# Revit family: IS_Connect_E5048_BIM_DE
name_source: partatom
category: Plumbing Fixtures
revit_build: Autodesk Revit 2016 (Build: 20150220_1215(x64)
units: mm (PartAtom-declared; Revit-internal decimal feet)

## family parameters
Cut with Voids When Loaded = Yes
Host = Face
OmniClass Number = 23.45.05.14.14
OmniClass Title = Sinks/Lavatories
Part Type = Normal
Room Calculation Point = No
Round Connector Dimension = Use Diameter
Shared = Yes

## types (1)
- E504801-Connect Oval 55cm under-countertop washbasin with overflow
    Accessories = www.idealstandard.de\ersatzteile
    AreaUnits = millimeters
    Assembly Code = C1030200
    AssetType = Fixed
    BIMObjectName = ISI_IdealStandard_Sinks_CONNECT_E504801
    BIMobject category = Basins
    BarCode = 5017830446910
    Brand url = http://www.idealstandard.co.uk
    CWFU = 0
    Category = SanitaryTerminal_WASHHANDBASIN_UK
    CodePerformance = DIN EN 14688 CL 15, DIN EN 31
    Color = White
    ConnectionType = Plumbing
    Cost = 0 $
    CurrencyUnit = €
    Date of publishing = 4/3/2017
    Default Elevation = 850 mm
    Description = Connect oval 55 cm under-countertop washbasin with overflow
    DrainSize = 32 mm
    DurationUnit = year
    EAN code = https://5017830446910
    Edition number = 1
    ExpectedLife = 25
    Features = CONNECT under countertop washbasin 550x380mm, no taphole, with overflow
    Finish = White
    GrossWeight = 8 kg
    HWFU = 0
    IfcExportAs = IfcSanitaryTerminalType
    IfcExportType = WASHHANDBASIN
    Installation instructions = http://www.idealstandard.de
    InstallationDate = 1900-12-31T23:59:59
    InstallationInstructions = www.idealstandard.de\produkte
    LinearUnits = millimeters
    Manufacturer name = Ideal Standard
    ManufacturerURL = www.idealstandard.de
    Material = Vitreous china
    Material main = Ceramics
    Model = E504801
    ModelNumber = E504801
    ModelReference = IS Unterbauwaschtisch CONNECT, oval, o.Hl., m.Ül., 550x380x175mm, Weiß
    NBSDescription = Undermounted wash basins
    NBSReference = 45-35-70/366
    Name = ISI_IdealStandard_Sinks_CONNECT_E504801
    NettWeight = 6,747 kg
    Nominal height = 175 mm
    Nominal width = 550 mm
    NominalDepth = 0 mm  [stored 0 ft]
    NominalLength = 380 mm
    Product Guid = 2755919d-d6bd-4df7-90a9-7ed34b0d341d
    Product SKU = E5048
    Product data url = https://bimobject.com
    Product family = CONNECT
    Product group = Basin
    Product url = http://www.idealstandard.de
    ProductInformation = www.idealstandard.de
    QR code = http://bimobject.com
    Shape = Sculptured
    Size = 550 x 380 x 193 mm
    Space = Internal
    SpareParts = www.idealstandard.de/ersatzteile
    Technical description = http://www.idealstandard.de
    URL = www.idealstandard.de
    Uniclass 2015 Code = Pr_40_20_96
    Uniclass 2015 Name = Wash basins, sinks and troughs
    Uniclass2015Code = Pr_40_20_96_18
    Uniclass2015Title = Counter top wash basin
    Uniclass2015Version = Products v1.1
    Version = 1
    VolumeUnits = Litres
    WFU = 0
    WashHandBasinMounting = Other
    WashHandBasinType = HandRinse
    Weight Net (Kg) = 6.75
    WorktopThickness = 18 mm

note: [stored X ft] marks values corroborated as IEEE doubles in the binary element streams (Revit-internal decimal feet)

## geometry (parser evidence)
native form markers: Blend x2, Sweep x2
no freeform markers — native parametric forms only
